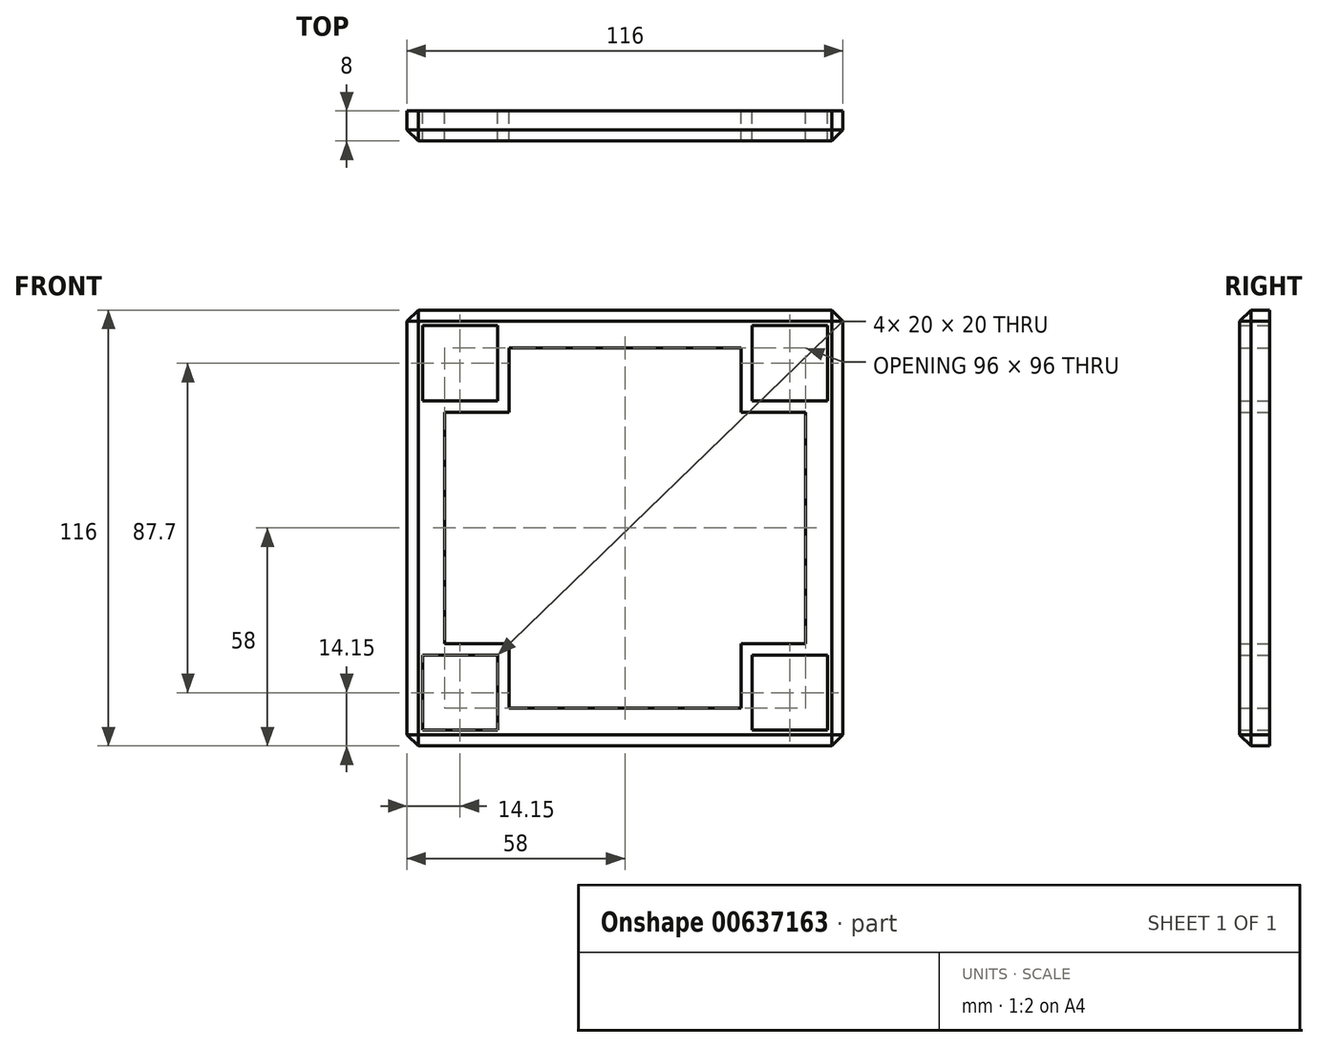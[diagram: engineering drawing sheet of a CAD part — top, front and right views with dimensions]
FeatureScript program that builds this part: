
annotation { "Feature Type Name" : "Feature", "Feature Type Description" : "" }
export const myFeature = defineFeature(function(context is Context, id is Id, definition is map)
    precondition{}
    {
        {
            var Q0;
            Q0=qCreatedBy(makeId("Front.planeOp"),FACE);
            var sketch = newSketch(context, id + "F0", { "sketchPlane" : qUnion([Q0])});
            skLineSegment(sketch, "E0.bottom", {"start": v(0, 0) * mm, "end": v(116, 0) * mm});
            skLineSegment(sketch, "E0.top", {"start": v(0, 116) * mm, "end": v(116, 116) * mm});
            skLineSegment(sketch, "E0.left", {"start": v(0, 0) * mm, "end": v(0, 116) * mm});
            skLineSegment(sketch, "E0.right", {"start": v(116, 0) * mm, "end": v(116, 116) * mm});
            skLineSegment(sketch, "E1.bottom", {"start": v(4.15, 111.85) * mm, "end": v(24.15, 111.85) * mm});
            skLineSegment(sketch, "E1.top", {"start": v(4.15, 91.85) * mm, "end": v(24.15, 91.85) * mm});
            skLineSegment(sketch, "E1.left", {"start": v(4.15, 111.85) * mm, "end": v(4.15, 91.85) * mm});
            skLineSegment(sketch, "E1.right", {"start": v(24.15, 111.85) * mm, "end": v(24.15, 91.85) * mm});
            skLineSegment(sketch, "E2.bottom", {"start": v(4.15, 4.15) * mm, "end": v(24.15, 4.15) * mm});
            skLineSegment(sketch, "E2.top", {"start": v(4.15, 24.15) * mm, "end": v(24.15, 24.15) * mm});
            skLineSegment(sketch, "E2.left", {"start": v(4.15, 4.15) * mm, "end": v(4.15, 24.15) * mm});
            skLineSegment(sketch, "E2.right", {"start": v(24.15, 4.15) * mm, "end": v(24.15, 24.15) * mm});
            skLineSegment(sketch, "E3.bottom", {"start": v(91.85, 24.15) * mm, "end": v(111.85, 24.15) * mm});
            skLineSegment(sketch, "E3.top", {"start": v(91.85, 4.15) * mm, "end": v(111.85, 4.15) * mm});
            skLineSegment(sketch, "E3.left", {"start": v(91.85, 24.15) * mm, "end": v(91.85, 4.15) * mm});
            skLineSegment(sketch, "E3.right", {"start": v(111.85, 24.15) * mm, "end": v(111.85, 4.15) * mm});
            skLineSegment(sketch, "E4.bottom", {"start": v(91.85, 111.85) * mm, "end": v(111.85, 111.85) * mm});
            skLineSegment(sketch, "E4.top", {"start": v(91.85, 91.85) * mm, "end": v(111.85, 91.85) * mm});
            skLineSegment(sketch, "E4.left", {"start": v(91.85, 111.85) * mm, "end": v(91.85, 91.85) * mm});
            skLineSegment(sketch, "E4.right", {"start": v(111.85, 111.85) * mm, "end": v(111.85, 91.85) * mm});
            skLineSegment(sketch, "E5", {"start": v(10, 27.15) * mm, "end": v(10, 88.85) * mm});
            skLineSegment(sketch, "E6", {"start": v(10, 88.85) * mm, "end": v(27.15, 88.85) * mm});
            skLineSegment(sketch, "E7", {"start": v(27.15, 88.85) * mm, "end": v(27.15, 106) * mm});
            skLineSegment(sketch, "E8", {"start": v(27.15, 106) * mm, "end": v(88.85, 106) * mm});
            skLineSegment(sketch, "E9", {"start": v(88.85, 106) * mm, "end": v(88.85, 88.85) * mm});
            skLineSegment(sketch, "E10", {"start": v(88.85, 88.85) * mm, "end": v(106, 88.85) * mm});
            skLineSegment(sketch, "E11", {"start": v(106, 88.85) * mm, "end": v(106, 27.15) * mm});
            skLineSegment(sketch, "E12", {"start": v(106, 27.15) * mm, "end": v(88.85, 27.15) * mm});
            skLineSegment(sketch, "E13", {"start": v(88.85, 27.15) * mm, "end": v(88.85, 10) * mm});
            skLineSegment(sketch, "E14", {"start": v(88.85, 10) * mm, "end": v(27.15, 10) * mm});
            skLineSegment(sketch, "E15", {"start": v(27.15, 10) * mm, "end": v(27.15, 27.15) * mm});
            skLineSegment(sketch, "E16", {"start": v(27.15, 27.15) * mm, "end": v(10, 27.15) * mm});
            skSolve(sketch);
        }
        {
            var Q0;
            Q0=makeQuery(id+"F0.imprint","IMPRINT",FACE,{"disambiguationData":[TD([[makeQuery(id+"F0.imprint","IMPRINT",EDGE,{"derivedFrom":sQuery(id+"F0.wireOp",EDGE,"E0.bottom")}),1.0]])]});
            extrude(context, id + "F1", {"entities" : qUnion([Q0]), "depth" : 8 * mm, "offsetDistance" : 25 * mm});
        }
        {
            var Q0;
            Q0=makeQuery(id+"F1.opExtrude","SWEPT_EDGE",EDGE,{"disambiguationData":[OSD([sQuery(id+"F0.wireOp",EDGE,"E0.bottom"),sQuery(id+"F0.wireOp",EDGE,"E0.left")])]});
            var Q1;
            Q1=makeQuery(id+"F1.opExtrude","SWEPT_EDGE",EDGE,{"disambiguationData":[OSD([sQuery(id+"F0.wireOp",EDGE,"E0.top"),sQuery(id+"F0.wireOp",EDGE,"E0.left")])]});
            var Q2;
            Q2=makeQuery(id+"F1.opExtrude","SWEPT_EDGE",EDGE,{"disambiguationData":[OSD([sQuery(id+"F0.wireOp",EDGE,"E0.top"),sQuery(id+"F0.wireOp",EDGE,"E0.right")])]});
            var Q3;
            Q3=makeQuery(id+"F1.opExtrude","SWEPT_EDGE",EDGE,{"disambiguationData":[OSD([sQuery(id+"F0.wireOp",EDGE,"E0.bottom"),sQuery(id+"F0.wireOp",EDGE,"E0.right")])]});
            var Q4;
            Q4=makeQuery(id+"F1.opExtrude","CAP_EDGE",EDGE,{"disambiguationData":[OSD([sQuery(id+"F0.wireOp",EDGE,"E0.right")])],"isStart":false});
            var Q5;
            Q5=makeQuery(id+"F1.opExtrude","CAP_EDGE",EDGE,{"disambiguationData":[OSD([sQuery(id+"F0.wireOp",EDGE,"E0.left")])],"isStart":false});
            var Q6;
            Q6=makeQuery(id+"F1.opExtrude","CAP_EDGE",EDGE,{"disambiguationData":[OSD([sQuery(id+"F0.wireOp",EDGE,"E0.bottom")])],"isStart":false});
            var Q7;
            Q7=makeQuery(id+"F1.opExtrude","CAP_EDGE",EDGE,{"disambiguationData":[OSD([sQuery(id+"F0.wireOp",EDGE,"E0.top")])],"isStart":false});
            chamfer(context, id + "F2", {"entities" : qUnion([Q0, Q1, Q2, Q3, Q4, Q5, Q6, Q7]), "width" : 3 * mm, "tangentPropagation" : true});
        }
    });
